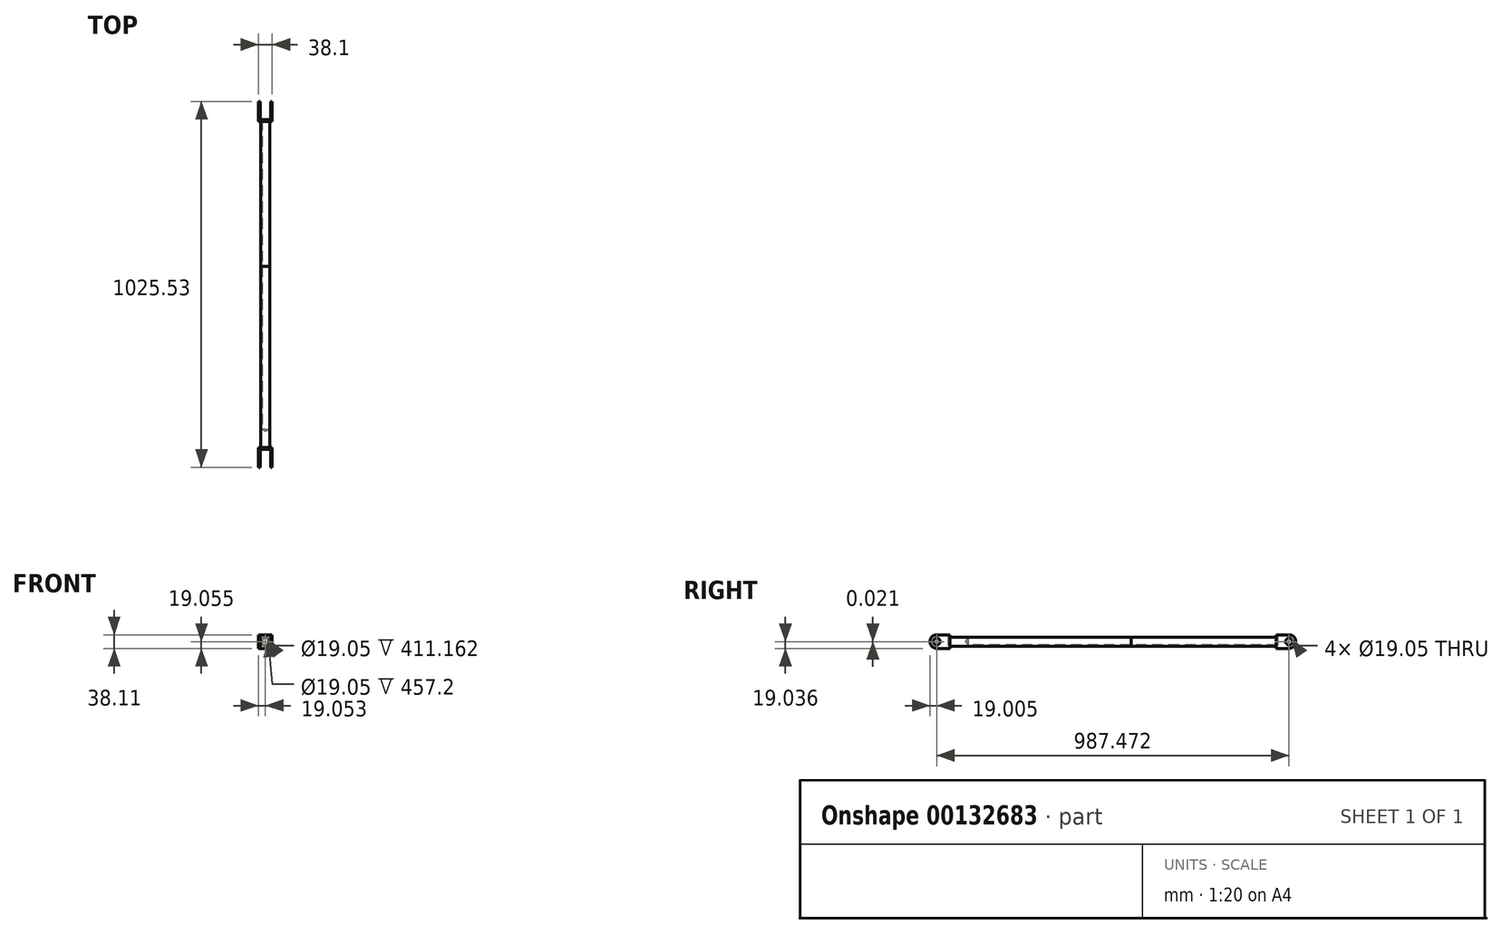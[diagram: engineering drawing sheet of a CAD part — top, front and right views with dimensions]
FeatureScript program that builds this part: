
annotation { "Feature Type Name" : "Feature", "Feature Type Description" : "" }
export const myFeature = defineFeature(function(context is Context, id is Id, definition is map)
    precondition{}
    {
        {
            var Q0;
            Q0=qCreatedBy(makeId("Right.planeOp"),FACE);
            var sketch = newSketch(context, id + "F0", { "sketchPlane" : qUnion([Q0])});
            skLineSegment(sketch, "E0.bottom", {"start": v(-173.45, 28.87) * mm, "end": v(-122.65, 28.87) * mm});
            skLineSegment(sketch, "E0.top", {"start": v(-173.45, -9.23) * mm, "end": v(-122.65, -9.23) * mm});
            skLineSegment(sketch, "E0.left", {"start": v(-173.45, 28.87) * mm, "end": v(-173.45, -9.23) * mm});
            skLineSegment(sketch, "E0.right", {"start": v(-122.65, 28.87) * mm, "end": v(-122.65, -9.23) * mm});
            skCircle(sketch, "E1", {"center": v(-154.4, 9.82) * mm, "radius": 9.53 * mm});
            skPoint(sketch, "E1.centerSnap0", {"position": v(-148.05, -9.23) * mm});
            skSolve(sketch);
        }
        {
            var Q0;
            Q0=makeQuery(id+"F0.imprint","IMPRINT",FACE,{"disambiguationData":[TD([[makeQuery(id+"F0.imprint","IMPRINT",EDGE,{"derivedFrom":sQuery(id+"F0.wireOp",EDGE,"E0.bottom")}),-1.0]])]});
            extrude(context, id + "F1", {"entities" : qUnion([Q0]), "depth" : 4.76 * mm});
        }
        {
            var Q0;
            Q0=makeQuery(id+"F1.opExtrude","SWEPT_EDGE",EDGE,{"disambiguationData":[OSD([sQuery(id+"F0.wireOp",EDGE,"E0.bottom"),sQuery(id+"F0.wireOp",EDGE,"E0.left")])]});
            var Q1;
            Q1=makeQuery(id+"F1.opExtrude","SWEPT_EDGE",EDGE,{"disambiguationData":[OSD([sQuery(id+"F0.wireOp",EDGE,"E0.top"),sQuery(id+"F0.wireOp",EDGE,"E0.left")])]});
            fillet(context, id + "F2", {"entities" : qUnion([Q0, Q1]), "radius" : 19.05 * mm, "tangentPropagation" : true, "allowEdgeOverflow" : false});
        }
        {
            var Q0;
            Q0=makeQuery(id+"F1.opExtrude","SWEPT_FACE",FACE,{"disambiguationData":[OSD([sQuery(id+"F0.wireOp",EDGE,"E0.right")])]});
            var sketch = newSketch(context, id + "F3", { "sketchPlane" : qUnion([Q0])});
            skLineSegment(sketch, "E2.bottom", {"start": v(-4.76, 28.87) * mm, "end": v(33.34, 28.87) * mm});
            skLineSegment(sketch, "E2.top", {"start": v(-4.76, -9.23) * mm, "end": v(33.34, -9.23) * mm});
            skLineSegment(sketch, "E2.left", {"start": v(-4.76, 28.87) * mm, "end": v(-4.76, -9.23) * mm});
            skLineSegment(sketch, "E2.right", {"start": v(33.34, 28.87) * mm, "end": v(33.34, -9.23) * mm});
            skSolve(sketch);
        }
        {
            var Q0;
            {var subQ2=sQuery(id+"F3.wireOp",EDGE,"E2.right");Q0=makeQuery(id+"F3.imprint","IMPRINT",FACE,{"disambiguationData":[TD([[makeQuery(id+"F3.imprint","IMPRINT",EDGE,{"derivedFrom":subQ2}),-1.0]])]});}
            var Q1;
            {var subQ2=sQuery(id+"F3.wireOp",EDGE,"E2.left");Q1=makeQuery(id+"F3.imprint","IMPRINT",FACE,{"disambiguationData":[TD([[makeQuery(id+"F3.imprint","IMPRINT",EDGE,{"derivedFrom":subQ2}),1.0]])]});}
            extrude(context, id + "F4", {"entities" : qUnion([Q0, Q1]), "operationType" : NewBodyOperationType.ADD, "depth" : 4.76 * mm});
        }
        {
            var Q0;
            Q0=makeQuery(id+"F4.opExtrude","SWEPT_FACE",FACE,{"disambiguationData":[OSD([sQuery(id+"F3.wireOp",EDGE,"E2.right")])]});
            var sketch = newSketch(context, id + "F5", { "sketchPlane" : qUnion([Q0])});
            skLineSegment(sketch, "E3.bottom", {"start": v(122.65, 28.87) * mm, "end": v(173.45, 28.87) * mm});
            skLineSegment(sketch, "E3.top", {"start": v(122.65, -9.23) * mm, "end": v(173.45, -9.23) * mm});
            skLineSegment(sketch, "E3.left", {"start": v(122.65, 28.87) * mm, "end": v(122.65, -9.23) * mm});
            skLineSegment(sketch, "E3.right", {"start": v(173.45, 28.87) * mm, "end": v(173.45, -9.23) * mm});
            skCircle(sketch, "E4", {"center": v(154.44, 9.8) * mm, "radius": 9.53 * mm});
            skSolve(sketch);
        }
        {
            var Q0;
            Q0=makeQuery(id+"F5.imprint","IMPRINT",FACE,{"disambiguationData":[TD([[makeQuery(id+"F5.imprint","IMPRINT",EDGE,{"derivedFrom":sQuery(id+"F5.wireOp",EDGE,"E3.bottom")}),-1.0]])]});
            extrude(context, id + "F6", {"entities" : qUnion([Q0]), "operationType" : NewBodyOperationType.ADD, "oppositeDirection" : true, "depth" : 4.76 * mm});
        }
        {
            var Q0;
            Q0=makeQuery(id+"F6.opExtrude","SWEPT_EDGE",EDGE,{"disambiguationData":[OSD([sQuery(id+"F5.wireOp",EDGE,"E3.bottom"),sQuery(id+"F5.wireOp",EDGE,"E3.right")])]});
            var Q1;
            Q1=makeQuery(id+"F6.opExtrude","SWEPT_EDGE",EDGE,{"disambiguationData":[OSD([sQuery(id+"F5.wireOp",EDGE,"E3.top"),sQuery(id+"F5.wireOp",EDGE,"E3.right")])]});
            fillet(context, id + "F7", {"entities" : qUnion([Q0, Q1]), "radius" : 19.05 * mm, "tangentPropagation" : true, "allowEdgeOverflow" : false});
        }
        {
            var Q0;
            Q0=makeQuery(id+"F4.opExtrude","CAP_FACE",FACE,{"disambiguationData":[OSD([sQuery(id+"F3.wireOp",EDGE,"E2.bottom"),sQuery(id+"F3.wireOp",EDGE,"E2.top"),sQuery(id+"F3.wireOp",EDGE,"E2.left"),sQuery(id+"F3.wireOp",EDGE,"E2.right")])],"isStart":false});
            var sketch = newSketch(context, id + "F8", { "sketchPlane" : qUnion([Q0])});
            skCircle(sketch, "E5", {"center": v(14.29, 9.82) * mm, "radius": 12.7 * mm});
            skPoint(sketch, "E6", {"position": v(33.34, 9.82) * mm});
            skPoint(sketch, "E7", {"position": v(14.29, -9.23) * mm});
            skSolve(sketch);
        }
        {
            var Q0;
            Q0=makeQuery(id+"F8.imprint","IMPRINT",FACE,{"disambiguationData":[TD([[makeQuery(id+"F8.imprint","IMPRINT",EDGE,{"derivedFrom":sQuery(id+"F8.wireOp",EDGE,"E5")}),1.0]])]});
            extrude(context, id + "F9", {"entities" : qUnion([Q0]), "operationType" : NewBodyOperationType.ADD, "flatOperationType" : FlatOperationType.REMOVE, "offsetDistance" : 25.4 * mm, "depth" : 508 * mm, "domain" : OperationDomain.MODEL});
        }
        {
            var Q0;
            Q0=makeQuery(id+"F9.opExtrude","CAP_FACE",FACE,{"disambiguationData":[OSD([sQuery(id+"F8.wireOp",EDGE,"E5")])],"isStart":false});
            var sketch = newSketch(context, id + "F10", { "sketchPlane" : qUnion([Q0])});
            skPoint(sketch, "E8", {"position": v(14.29, 9.82) * mm});
            skSolve(sketch);
        }
        {
            var Q0;
            Q0=sQuery(id+"F10.wireOp",VERTEX,"E8");
            var Q1;
            Q1=makeQuery(id+"F1.opExtrude","SWEPT_BODY",BODY,{"disambiguationData":[OSD([sQuery(id+"F0.wireOp",EDGE,"E0.bottom"),sQuery(id+"F0.wireOp",EDGE,"E0.top"),sQuery(id+"F0.wireOp",EDGE,"E0.left"),sQuery(id+"F0.wireOp",EDGE,"E0.right"),sQuery(id+"F0.wireOp",EDGE,"E1")])]});
            hole(context, id + "F11", {"style" : HoleStyle.SIMPLE, "endStyle" : HoleEndStyle.BLIND, "holeDiameter" : 19.05 * mm, "holeDepth" : 457.2 * mm, "startFromSketch" : true, "locations" : qUnion([Q0]), "scope" : qUnion([Q1])});
        }
        {
            var Q0;
            Q0=makeQuery(id+"F9.opExtrude","CAP_FACE",FACE,{"disambiguationData":[OSD([sQuery(id+"F8.wireOp",EDGE,"E5")])],"isStart":false});
            var sketch = newSketch(context, id + "F12", { "sketchPlane" : qUnion([Q0])});
            skCircle(sketch, "E9", {"center": v(14.29, 9.82) * mm, "radius": 9.53 * mm});
            skSolve(sketch);
        }
        {
            var Q0;
            Q0=makeQuery(id+"F12.imprint","IMPRINT",FACE,{"disambiguationData":[TD([[makeQuery(id+"F12.imprint","IMPRINT",EDGE,{"derivedFrom":sQuery(id+"F12.wireOp",EDGE,"E9")}),1.0]])]});
            extrude(context, id + "F13", {"entities" : qUnion([Q0]), "depth" : 406.4 * mm});
        }
        {
            var Q0;
            Q0=makeQuery(id+"F13.opExtrude","CAP_FACE",FACE,{"disambiguationData":[OSD([sQuery(id+"F12.wireOp",EDGE,"E9")])],"isStart":false});
            var sketch = newSketch(context, id + "F14", { "sketchPlane" : qUnion([Q0])});
            skLineSegment(sketch, "E10.bottom", {"start": v(-4.76, 28.88) * mm, "end": v(33.34, 28.88) * mm});
            skLineSegment(sketch, "E10.top", {"start": v(-4.76, -9.22) * mm, "end": v(33.34, -9.22) * mm});
            skLineSegment(sketch, "E10.left", {"start": v(-4.76, 28.88) * mm, "end": v(-4.76, -9.22) * mm});
            skLineSegment(sketch, "E10.right", {"start": v(33.34, 28.88) * mm, "end": v(33.34, -9.22) * mm});
            skSolve(sketch);
        }
        {
            var Q0;
            Q0=makeQuery(id+"F14.imprint","IMPRINT",FACE,{"disambiguationData":[TD([[makeQuery(id+"F14.imprint","IMPRINT",EDGE,{"derivedFrom":sQuery(id+"F14.wireOp",EDGE,"E10.bottom")}),-1.0]])]});
            var Q1;
            Q1=makeQuery(id+"F14.imprint","IMPRINT",FACE,{"disambiguationData":[TD([[makeQuery(id+"F14.imprint","IMPRINT",EDGE,{"derivedFrom":makeQuery(id+"F13.opExtrude","CAP_EDGE",EDGE,{"disambiguationData":[OSD([sQuery(id+"F12.wireOp",EDGE,"E9")])],"isStart":false})}),1.0]])]});
            extrude(context, id + "F15", {"entities" : qUnion([Q0, Q1]), "operationType" : NewBodyOperationType.ADD, "depth" : 4.76 * mm});
        }
        {
            var Q0;
            Q0=makeQuery(id+"F15.opExtrude","SWEPT_FACE",FACE,{"disambiguationData":[OSD([sQuery(id+"F14.wireOp",EDGE,"E10.left")])]});
            var sketch = newSketch(context, id + "F16", { "sketchPlane" : qUnion([Q0])});
            skLineSegment(sketch, "E11.bottom", {"start": v(801.28, 28.88) * mm, "end": v(852.08, 28.88) * mm});
            skLineSegment(sketch, "E11.top", {"start": v(801.28, -9.22) * mm, "end": v(852.08, -9.22) * mm});
            skLineSegment(sketch, "E11.left", {"start": v(801.28, 28.88) * mm, "end": v(801.28, -9.22) * mm});
            skLineSegment(sketch, "E11.right", {"start": v(852.08, 28.88) * mm, "end": v(852.08, -9.22) * mm});
            skCircle(sketch, "E12", {"center": v(833.03, 9.83) * mm, "radius": 9.53 * mm});
            skPoint(sketch, "E12.centerSnap0", {"position": v(852.08, 9.83) * mm});
            skPoint(sketch, "E12.centerSnap1", {"position": v(826.68, -9.22) * mm});
            skSolve(sketch);
        }
        {
            var Q0;
            Q0=makeQuery(id+"F16.imprint","IMPRINT",FACE,{"disambiguationData":[TD([[makeQuery(id+"F16.imprint","IMPRINT",EDGE,{"derivedFrom":sQuery(id+"F16.wireOp",EDGE,"E11.bottom")}),-1.0]])]});
            extrude(context, id + "F17", {"entities" : qUnion([Q0]), "operationType" : NewBodyOperationType.ADD, "oppositeDirection" : true, "depth" : 4.76 * mm});
        }
        {
            var Q0;
            Q0=makeQuery(id+"F17.opExtrude","SWEPT_EDGE",EDGE,{"disambiguationData":[OSD([sQuery(id+"F16.wireOp",EDGE,"E11.bottom"),sQuery(id+"F16.wireOp",EDGE,"E11.right")])]});
            var Q1;
            Q1=makeQuery(id+"F17.opExtrude","SWEPT_EDGE",EDGE,{"disambiguationData":[OSD([sQuery(id+"F16.wireOp",EDGE,"E11.top"),sQuery(id+"F16.wireOp",EDGE,"E11.right")])]});
            fillet(context, id + "F18", {"entities" : qUnion([Q0, Q1]), "radius" : 19.05 * mm, "tangentPropagation" : true, "allowEdgeOverflow" : false});
        }
        {
            var Q0;
            Q0=makeQuery(id+"F15.opExtrude","SWEPT_FACE",FACE,{"disambiguationData":[OSD([sQuery(id+"F14.wireOp",EDGE,"E10.right")])]});
            var sketch = newSketch(context, id + "F19", { "sketchPlane" : qUnion([Q0])});
            skLineSegment(sketch, "E13.bottom", {"start": v(-801.28, 28.88) * mm, "end": v(-852.08, 28.88) * mm});
            skLineSegment(sketch, "E13.top", {"start": v(-801.28, -9.22) * mm, "end": v(-852.08, -9.22) * mm});
            skLineSegment(sketch, "E13.left", {"start": v(-801.28, 28.88) * mm, "end": v(-801.28, -9.22) * mm});
            skLineSegment(sketch, "E13.right", {"start": v(-852.08, 28.88) * mm, "end": v(-852.08, -9.22) * mm});
            skCircle(sketch, "E14", {"center": v(-833.03, 9.83) * mm, "radius": 9.53 * mm});
            skSolve(sketch);
        }
        {
            var Q0;
            Q0=makeQuery(id+"F19.imprint","IMPRINT",FACE,{"disambiguationData":[TD([[makeQuery(id+"F19.imprint","IMPRINT",EDGE,{"derivedFrom":sQuery(id+"F19.wireOp",EDGE,"E13.bottom")}),1.0]])]});
            extrude(context, id + "F20", {"entities" : qUnion([Q0]), "operationType" : NewBodyOperationType.ADD, "oppositeDirection" : true, "depth" : 4.76 * mm});
        }
        {
            var Q0;
            Q0=makeQuery(id+"F20.opExtrude","SWEPT_EDGE",EDGE,{"disambiguationData":[OSD([sQuery(id+"F19.wireOp",EDGE,"E13.bottom"),sQuery(id+"F19.wireOp",EDGE,"E13.right")])]});
            var Q1;
            Q1=makeQuery(id+"F20.opExtrude","SWEPT_EDGE",EDGE,{"disambiguationData":[OSD([sQuery(id+"F19.wireOp",EDGE,"E13.top"),sQuery(id+"F19.wireOp",EDGE,"E13.right")])]});
            fillet(context, id + "F21", {"entities" : qUnion([Q0, Q1]), "radius" : 19.05 * mm, "tangentPropagation" : true, "allowEdgeOverflow" : false});
        }
    });
